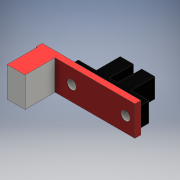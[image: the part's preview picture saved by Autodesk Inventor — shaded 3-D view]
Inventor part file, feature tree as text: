
AUTODESK INVENTOR PART (.ipt)
format: ipt  version: 2016 SP1 (Build 200210100, 210)  size: 157,184 bytes
history: native  units: mm
features: extrude x4, sketch x4
ambient origin geometry x8: Origin, YZ Plane, XZ Plane, XY Plane, X Axis, Y Axis, Z Axis, Center Point
bodies: Solid1 (feature_tree)
feature tree (8):
  extrude  "Extrusion1"  Depth=6.0mm
  extrude  "Extrusion2"  Depth=4.4mm
  extrude  "Extrusion3"  Depth=4.4mm
  extrude  "Extrusion4"  Depth=10.0mm
  sketch  "Sketch1"  dims[d0=3.0mm d1=6.0mm]
  sketch  "Sketch2"  dims[d2=8.0mm d3=4.4mm]
  sketch  "Sketch3"  dims[d4=2.8mm d5=4.4mm]
  sketch  "Sketch4"  dims[d6=6.0mm d7=1.4mm d8=0.0mm d9=6.5mm d10=0.0mm d11=3.0mm d12=3.0mm d13=18.0mm d14=23.6mm d15=2.8mm d16=6.5mm d17=3.25mm d18=3.25mm d19=6.5mm d20=0.0mm d21=10.0mm d22=33.0mm d23=0.3mm d24=6.5mm d25=1.75mm d26=2.0mm d27=0.0mm d28=10.0mm d29=6.0mm d30=0.0mm d31=0.3mm d32=10.0mm d33=0.0mm]
